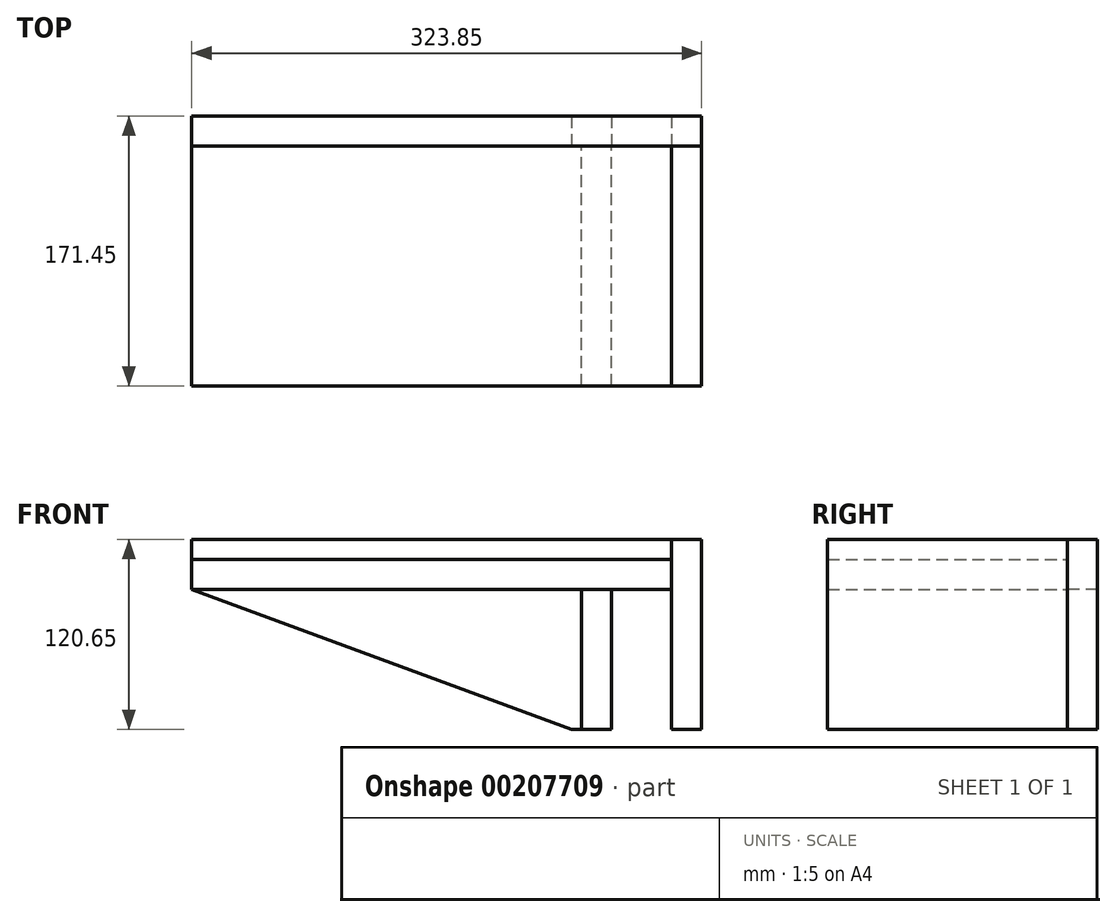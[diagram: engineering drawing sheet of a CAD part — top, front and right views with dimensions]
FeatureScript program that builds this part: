
annotation { "Feature Type Name" : "Feature", "Feature Type Description" : "" }
export const myFeature = defineFeature(function(context is Context, id is Id, definition is map)
    precondition{}
    {
        {
            var Q0;
            Q0=qCreatedBy(makeId("Front.planeOp"),FACE);
            var sketch = newSketch(context, id + "F0", { "sketchPlane" : qUnion([Q0])});
            skLineSegment(sketch, "E0", {"start": v(0, 0) * mm, "end": v(0, 120.65) * mm});
            skLineSegment(sketch, "E1", {"start": v(0, 120.65) * mm, "end": v(-330.2, 120.65) * mm});
            skLineSegment(sketch, "E2", {"start": v(-330.2, 120.65) * mm, "end": v(-330.2, 88.9) * mm});
            skLineSegment(sketch, "E3", {"start": v(-330.2, 88.9) * mm, "end": v(-88.9, 0) * mm});
            skLineSegment(sketch, "E4", {"start": v(-88.9, 0) * mm, "end": v(-63.5, 0) * mm});
            skLineSegment(sketch, "E5", {"start": v(-63.5, 0) * mm, "end": v(-63.5, 88.9) * mm});
            skLineSegment(sketch, "E6", {"start": v(-63.5, 88.9) * mm, "end": v(-25.4, 88.9) * mm});
            skLineSegment(sketch, "E7", {"start": v(-25.4, 88.9) * mm, "end": v(-25.4, 0) * mm});
            skLineSegment(sketch, "E8", {"start": v(-25.4, 0) * mm, "end": v(0, 0) * mm});
            skLineSegment(sketch, "E9", {"start": v(-25.4, 88.9) * mm, "end": v(-25.4, 107.95) * mm});
            skLineSegment(sketch, "E10", {"start": v(-25.4, 107.95) * mm, "end": v(-330.2, 107.95) * mm});
            skLineSegment(sketch, "E11", {"start": v(-63.5, 88.9) * mm, "end": v(-330.2, 88.9) * mm});
            skLineSegment(sketch, "E12", {"start": v(-82.55, 0) * mm, "end": v(-82.55, 88.9) * mm});
            skLineSegment(sketch, "E13", {"start": v(-6.35, 0) * mm, "end": v(-6.35, 120.65) * mm});
            skLineSegment(sketch, "E14", {"start": v(-25.4, 107.95) * mm, "end": v(-25.4, 120.65) * mm});
            skSolve(sketch);
        }
        {
            var Q0;
            {var subQ1=sQuery(id+"F0.wireOp",EDGE,"E6");Q0=makeQuery(id+"F0.imprint","IMPRINT",FACE,{"disambiguationData":[TD([[makeQuery(id+"F0.imprint","IMPRINT",EDGE,{"derivedFrom":subQ1}),1.0]])]});}
            extrude(context, id + "F1", {"entities" : qUnion([Q0]), "depth" : 152.4 * mm});
        }
        {
            var Q0;
            {var subQ0=sQuery(id+"F0.wireOp",EDGE,"E5");Q0=makeQuery(id+"F0.imprint","IMPRINT",FACE,{"disambiguationData":[TD([[makeQuery(id+"F0.imprint","IMPRINT",EDGE,{"derivedFrom":subQ0}),1.0]])]});}
            var Q1;
            Q1=makeQuery(id+"F1.opExtrude","CAP_FACE",FACE,{"disambiguationData":[OSD([sQuery(id+"F0.wireOp",EDGE,"E2"),sQuery(id+"F0.wireOp",EDGE,"E6"),sQuery(id+"F0.wireOp",EDGE,"E9"),sQuery(id+"F0.wireOp",EDGE,"E10"),sQuery(id+"F0.wireOp",EDGE,"E11")])],"isStart":false});
            extrude(context, id + "F2", {"entities" : qUnion([Q0]), "endBound" : BoundingType.UP_TO_SURFACE, "endBoundEntityFace" : qUnion([Q1]), "depth" : 25.4 * mm});
        }
        {
            var Q0;
            {var subQ1=sQuery(id+"F0.wireOp",EDGE,"E7");Q0=makeQuery(id+"F0.imprint","IMPRINT",FACE,{"disambiguationData":[TD([[makeQuery(id+"F0.imprint","IMPRINT",EDGE,{"derivedFrom":subQ1}),1.0]])]});}
            var Q1;
            Q1=makeQuery(id+"F1.opExtrude","CAP_FACE",FACE,{"disambiguationData":[OSD([sQuery(id+"F0.wireOp",EDGE,"E2"),sQuery(id+"F0.wireOp",EDGE,"E6"),sQuery(id+"F0.wireOp",EDGE,"E9"),sQuery(id+"F0.wireOp",EDGE,"E10"),sQuery(id+"F0.wireOp",EDGE,"E11")])],"isStart":false});
            extrude(context, id + "F3", {"entities" : qUnion([Q0]), "endBound" : BoundingType.UP_TO_SURFACE, "endBoundEntityFace" : qUnion([Q1]), "depth" : 25.4 * mm});
        }
        {
            var Q0;
            {var subQ4=sQuery(id+"F0.wireOp",EDGE,"E10");Q0=makeQuery(id+"F0.imprint","IMPRINT",FACE,{"disambiguationData":[TD([[makeQuery(id+"F0.imprint","IMPRINT",EDGE,{"derivedFrom":subQ4}),-1.0]])]});}
            var Q1;
            {var subQ1=sQuery(id+"F0.wireOp",EDGE,"E6");Q1=makeQuery(id+"F0.imprint","IMPRINT",FACE,{"disambiguationData":[TD([[makeQuery(id+"F0.imprint","IMPRINT",EDGE,{"derivedFrom":subQ1}),1.0]])]});}
            var Q2;
            {var subQ0=sQuery(id+"F0.wireOp",EDGE,"E3");Q2=makeQuery(id+"F0.imprint","IMPRINT",FACE,{"disambiguationData":[TD([[makeQuery(id+"F0.imprint","IMPRINT",EDGE,{"derivedFrom":subQ0}),1.0]])]});}
            var Q3;
            {var subQ0=sQuery(id+"F0.wireOp",EDGE,"E5");Q3=makeQuery(id+"F0.imprint","IMPRINT",FACE,{"disambiguationData":[TD([[makeQuery(id+"F0.imprint","IMPRINT",EDGE,{"derivedFrom":subQ0}),1.0]])]});}
            var Q4;
            {var subQ1=sQuery(id+"F0.wireOp",EDGE,"E7");Q4=makeQuery(id+"F0.imprint","IMPRINT",FACE,{"disambiguationData":[TD([[makeQuery(id+"F0.imprint","IMPRINT",EDGE,{"derivedFrom":subQ1}),1.0]])]});}
            extrude(context, id + "F4", {"entities" : qUnion([Q0, Q1, Q2, Q3, Q4]), "oppositeDirection" : true, "depth" : 19.05 * mm});
        }
    });
